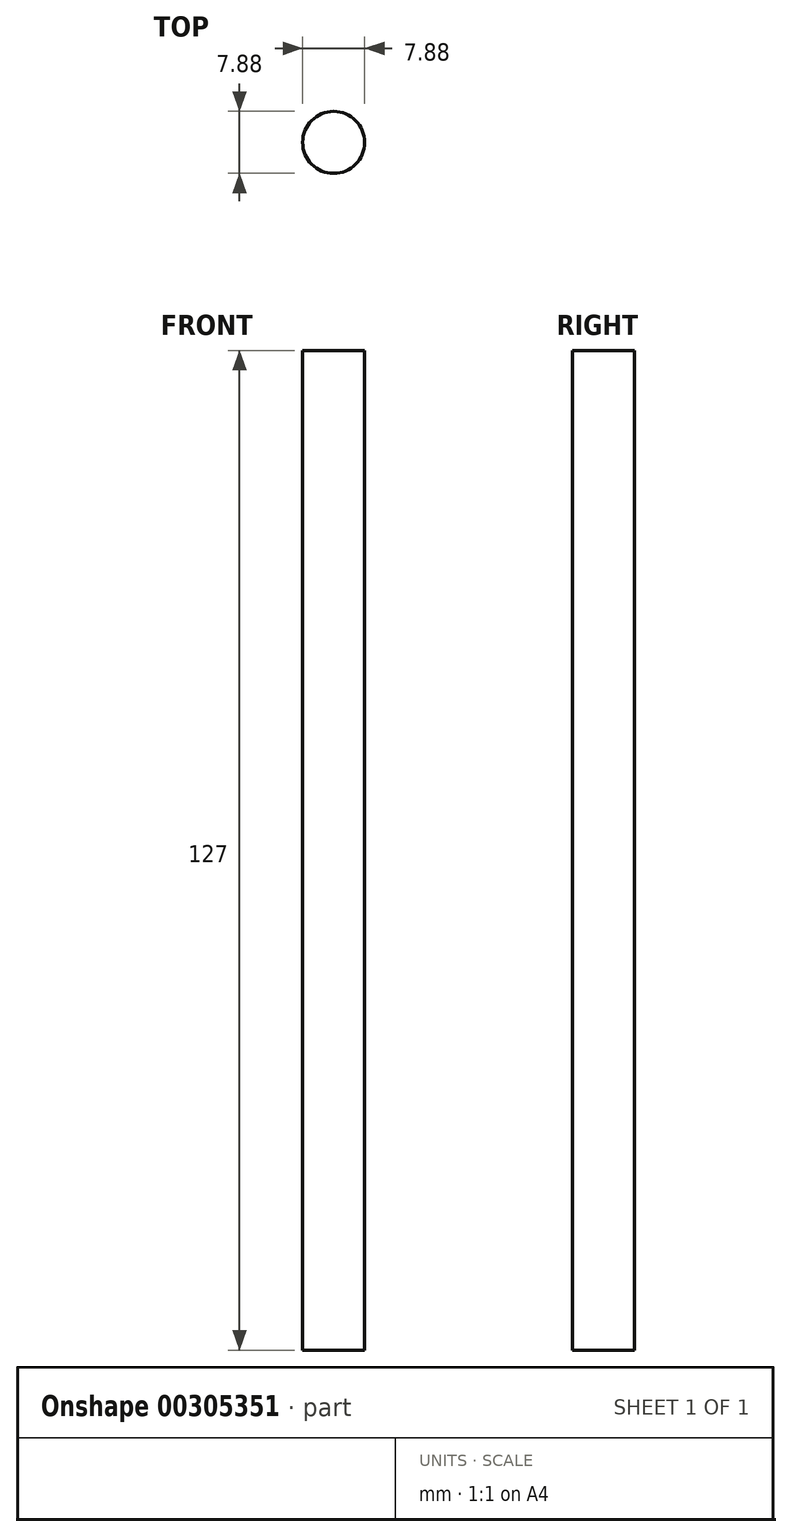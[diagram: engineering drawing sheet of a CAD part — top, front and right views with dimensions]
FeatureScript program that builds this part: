
annotation { "Feature Type Name" : "Feature", "Feature Type Description" : "" }
export const myFeature = defineFeature(function(context is Context, id is Id, definition is map)
    precondition{}
    {
        {
            var Q0;
            Q0=qCreatedBy(makeId("Top.planeOp"),FACE);
            var sketch = newSketch(context, id + "F0", { "sketchPlane" : qUnion([Q0])});
            skCircle(sketch, "E0", {"center": v(0, 0) * mm, "radius": 3.94 * mm});
            skSolve(sketch);
        }
        {
            var Q0;
            Q0=makeQuery(id+"F0.imprint","IMPRINT",FACE,{"disambiguationData":[TD([[makeQuery(id+"F0.imprint","IMPRINT",EDGE,{"derivedFrom":sQuery(id+"F0.wireOp",EDGE,"E0")}),1.0]])]});
            extrude(context, id + "F1", {"entities" : qUnion([Q0]), "depth" : 127 * mm});
        }
    });
